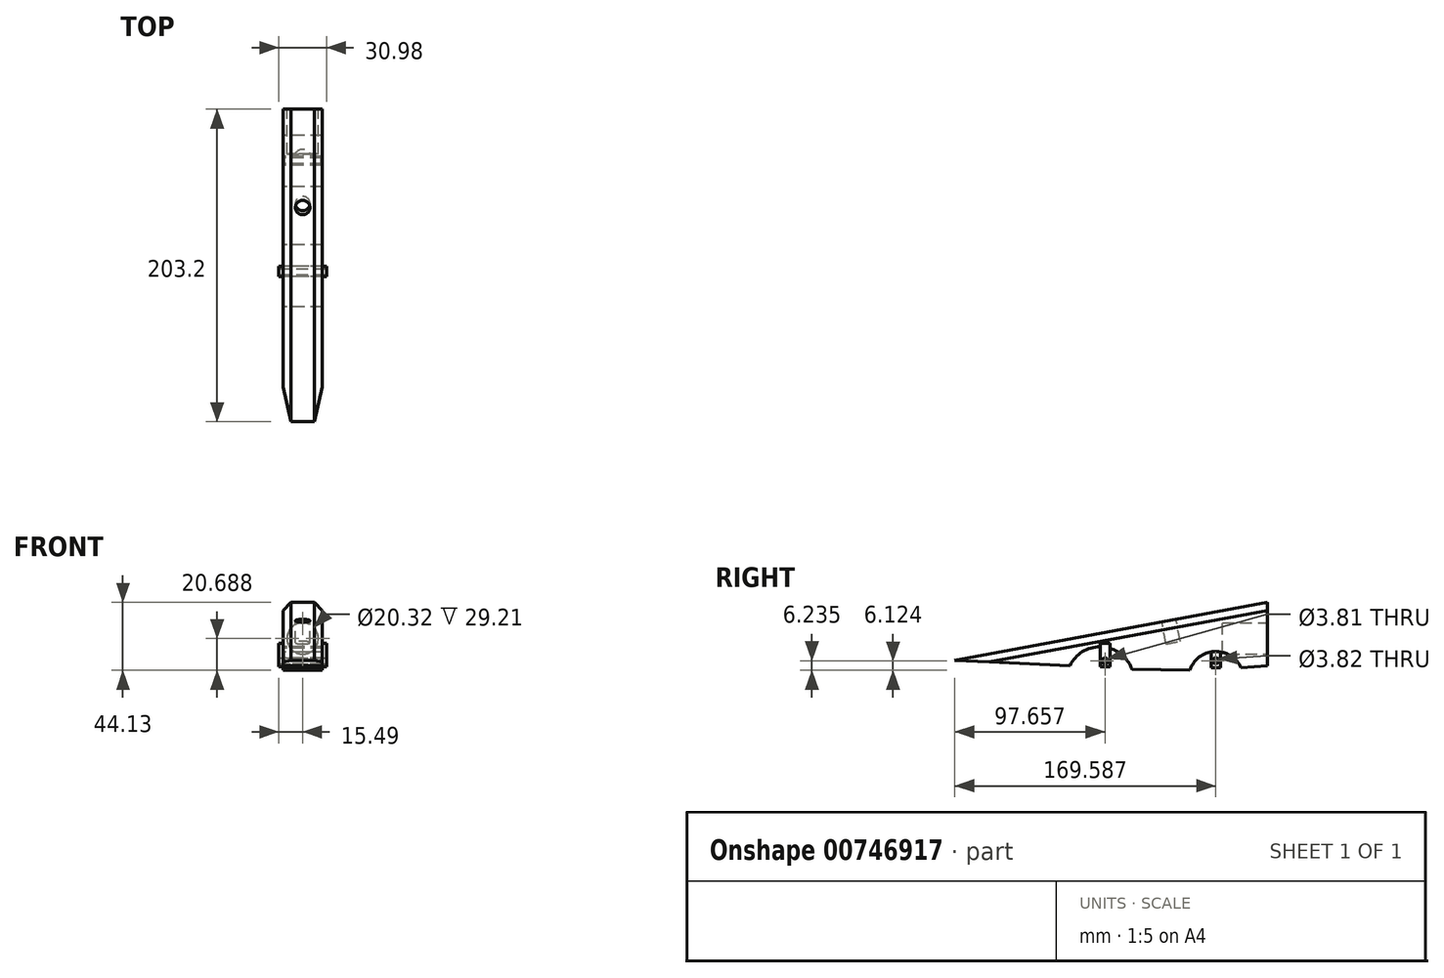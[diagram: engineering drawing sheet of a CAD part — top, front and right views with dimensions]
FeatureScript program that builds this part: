
annotation { "Feature Type Name" : "Feature", "Feature Type Description" : "" }
export const myFeature = defineFeature(function(context is Context, id is Id, definition is map)
    precondition{}
    {
        {
            var Q0;
            Q0=qCreatedBy(makeId("Right.planeOp"),FACE);
            var sketch = newSketch(context, id + "F0", { "sketchPlane" : qUnion([Q0])});
            skLineSegment(sketch, "E0", {"start": v(-100.94, -24.56) * mm, "end": v(102.26, 13.2) * mm});
            skLineSegment(sketch, "E1", {"start": v(102.26, 13.2) * mm, "end": v(102.26, -27.95) * mm});
            skArc(sketch, "E2", {"start": v(14.15, -30.28) * mm, "mid": v(-5.16, -15.67) * mm, "end": v(-26.12, -27.8) * mm});
            skArc(sketch, "E3", {"start": v(85.1, -29.1) * mm, "mid": v(67.81, -18.7) * mm, "end": v(51.76, -30.93) * mm});
            skLineSegment(sketch, "E4", {"start": v(-100.94, -24.56) * mm, "end": v(-26.12, -27.8) * mm});
            skLineSegment(sketch, "E5", {"start": v(14.15, -30.28) * mm, "end": v(51.76, -30.93) * mm});
            skLineSegment(sketch, "E6", {"start": v(85.1, -29.1) * mm, "end": v(102.26, -27.95) * mm});
            skSolve(sketch);
        }
        {
            var Q0;
            Q0 = qSketchRegion(id + "F0", true);
            extrude(context, id + "F1", {"entities" : qUnion([Q0]), "depth" : 12.7 * mm, "offsetDistance" : 25.4 * mm, "hasSecondDirection" : true, "secondDirectionOppositeDirection" : true, "secondDirectionDepth" : 12.7 * mm});
        }
        {
            var Q0;
            Q0=makeQuery(id+"F1.opExtrude","CAP_EDGE",EDGE,{"disambiguationData":[OSD([sQuery(id+"F0.wireOp",EDGE,"E0")])],"isStart":false});
            var Q1;
            Q1=makeQuery(id+"F1.opExtrude","CAP_EDGE",EDGE,{"disambiguationData":[OSD([sQuery(id+"F0.wireOp",EDGE,"E0")])],"isStart":true});
            chamfer(context, id + "F2", {"entities" : qUnion([Q0, Q1]), "width" : 5.08 * mm, "tangentPropagation" : true});
        }
        {
            var Q0;
            Q0=makeQuery(id+"F1.opExtrude","SWEPT_FACE",FACE,{"disambiguationData":[OSD([sQuery(id+"F0.wireOp",EDGE,"E1")])]});
            var sketch = newSketch(context, id + "F3", { "sketchPlane" : qUnion([Q0])});
            skCircle(sketch, "E7", {"center": v(0, -10.24) * mm, "radius": 10.16 * mm});
            skSolve(sketch);
        }
        {
            var Q0;
            Q0 = qSketchRegion(id + "F3", true);
            extrude(context, id + "F4", {"entities" : qUnion([Q0]), "operationType" : NewBodyOperationType.REMOVE, "oppositeDirection" : true, "depth" : 29.2 * mm, "offsetDistance" : 25.4 * mm});
        }
        {
            var Q0;
            Q0=makeQuery(id+"F1.opExtrude","SWEPT_FACE",FACE,{"disambiguationData":[OSD([sQuery(id+"F0.wireOp",EDGE,"E0")])]});
            var sketch = newSketch(context, id + "F5", { "sketchPlane" : qUnion([Q0])});
            skCircle(sketch, "E8", {"center": v(0, 37.9) * mm, "radius": 4.72 * mm});
            skSolve(sketch);
        }
        {
            var Q0;
            Q0 = qSketchRegion(id + "F5", true);
            extrude(context, id + "F6", {"entities" : qUnion([Q0]), "operationType" : NewBodyOperationType.REMOVE, "oppositeDirection" : true, "depth" : 14.48 * mm, "offsetDistance" : 25.4 * mm});
        }
        {
            var Q0;
            Q0=qCreatedBy(makeId("Right.planeOp"),FACE);
            var sketch = newSketch(context, id + "F7", { "sketchPlane" : qUnion([Q0])});
            skLineSegment(sketch, "E9.bottom", {"start": v(-6.41, -13.48) * mm, "end": v(0, -13.48) * mm});
            skLineSegment(sketch, "E9.top", {"start": v(-6.41, -28.58) * mm, "end": v(0, -28.58) * mm});
            skLineSegment(sketch, "E9.left", {"start": v(-6.41, -13.48) * mm, "end": v(-6.41, -28.58) * mm});
            skLineSegment(sketch, "E9.right", {"start": v(0, -13.48) * mm, "end": v(0, -28.58) * mm});
            skSolve(sketch);
        }
        {
            var Q0;
            Q0 = qSketchRegion(id + "F7", true);
            extrude(context, id + "F8", {"entities" : qUnion([Q0]), "operationType" : NewBodyOperationType.ADD, "depth" : 15.5 * mm, "offsetDistance" : 25.4 * mm, "hasSecondDirection" : true, "secondDirectionOppositeDirection" : true, "secondDirectionDepth" : 15.5 * mm});
        }
        {
            var Q0;
            Q0=makeQuery(id+"F8.opExtrude","CAP_FACE",FACE,{"disambiguationData":[OSD([sQuery(id+"F7.wireOp",EDGE,"E9.bottom"),sQuery(id+"F7.wireOp",EDGE,"E9.top"),sQuery(id+"F7.wireOp",EDGE,"E9.left"),sQuery(id+"F7.wireOp",EDGE,"E9.right")])],"isStart":false});
            var sketch = newSketch(context, id + "F9", { "sketchPlane" : qUnion([Q0])});
            skCircle(sketch, "E10", {"center": v(-3.28, -24.8) * mm, "radius": 1.9 * mm});
            skSolve(sketch);
        }
        {
            var Q0;
            Q0 = qSketchRegion(id + "F9", true);
            extrude(context, id + "F10", {"entities" : qUnion([Q0]), "operationType" : NewBodyOperationType.REMOVE, "oppositeDirection" : true, "depth" : 39.88 * mm, "offsetDistance" : 25.4 * mm});
        }
        {
            var Q0;
            Q0=qCreatedBy(makeId("Right.planeOp"),FACE);
            var sketch = newSketch(context, id + "F11", { "sketchPlane" : qUnion([Q0])});
            skLineSegment(sketch, "E11.bottom", {"start": v(65.7, -12.67) * mm, "end": v(71.72, -12.67) * mm});
            skLineSegment(sketch, "E11.top", {"start": v(65.7, -29.29) * mm, "end": v(71.72, -29.29) * mm});
            skLineSegment(sketch, "E11.left", {"start": v(65.7, -12.67) * mm, "end": v(65.7, -29.29) * mm});
            skLineSegment(sketch, "E11.right", {"start": v(71.72, -12.67) * mm, "end": v(71.72, -29.29) * mm});
            skSolve(sketch);
        }
        {
            var Q0;
            Q0 = qSketchRegion(id + "F11", true);
            extrude(context, id + "F12", {"entities" : qUnion([Q0]), "operationType" : NewBodyOperationType.ADD, "depth" : 12.2 * mm, "offsetDistance" : 25.4 * mm, "hasSecondDirection" : true, "secondDirectionOppositeDirection" : true, "secondDirectionDepth" : 12.2 * mm});
        }
        {
            var Q0;
            Q0=makeQuery(id+"F12.opExtrude","CAP_FACE",FACE,{"disambiguationData":[OSD([sQuery(id+"F11.wireOp",EDGE,"E11.bottom"),sQuery(id+"F11.wireOp",EDGE,"E11.top"),sQuery(id+"F11.wireOp",EDGE,"E11.left"),sQuery(id+"F11.wireOp",EDGE,"E11.right")])],"isStart":true});
            var sketch = newSketch(context, id + "F13", { "sketchPlane" : qUnion([Q0])});
            skPoint(sketch, "E12", {"position": v(-71.72, -24.1) * mm});
            skCircle(sketch, "E13", {"center": v(-68.65, -24.7) * mm, "radius": 1.9 * mm});
            skSolve(sketch);
        }
        {
            var Q0;
            Q0 = qSketchRegion(id + "F13", true);
            extrude(context, id + "F14", {"entities" : qUnion([Q0]), "operationType" : NewBodyOperationType.REMOVE, "oppositeDirection" : true, "depth" : 25.4 * mm, "offsetDistance" : 25.4 * mm});
        }
    });
